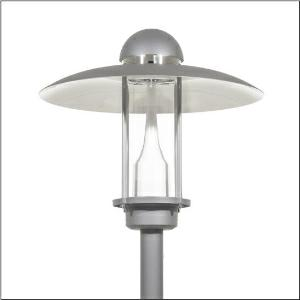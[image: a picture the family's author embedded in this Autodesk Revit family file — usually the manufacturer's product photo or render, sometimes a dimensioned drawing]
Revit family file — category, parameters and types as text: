
# Revit family: city-light_elegance_iq___st1_2a_5xa5265ef14h_e69b
name_source: partatom
category: Lighting Fixtures
units: mm (PartAtom-declared; Revit-internal decimal feet)

## family parameters
Cut with Voids When Loaded = No
Host = Face
Light Source = No
Part Type = Normal
Room Calculation Point = No
Round Connector Dimension = Use Diameter
Shared = No

## types (1)
- --- (1 x LED, 1470 lm, 10.5 W, 3000K)
    Apparent Load = 11 VA
    CIE Flux Codes = 22 62 94 98 100
    Color Rendering = 70
    Color Temperature = 3000K
    Default Elevation = 1800 mm
    Description = City-Light Elegance iQ, mast luminaire, Module 540 iQ-SR, primary light control with 3 zone facetted reflector, of plastic, silver coated, highly specular, structured, primary optical cover: cover, of PMMA, transparent, light distribution: ST1.2a, light emission: direct distribution, primary light characteristic: asymmetric, installation type: post-top, LED, High Power LED, rated luminous flux: 1.470lm, luminous efficacy: 140lm/W, light colour: 730, colour temperature: 3000K, control gear: ECG iQ, control: Auto-Match, Temp-Guard, Lumen-Switch, Night-Set, Smart-Wire, Light-Fading, Desk-Remote (wireless, voltage-free reading and setting of iQ features in the workshop via application-optimized NFC function/RFID function), optimised constant luminous flux control (CLO 2.0), Street-Remote, presetting dimming logarithmic, with terminal, 6-pole, max. 2.5mm², mains connection: 230..240V, AC, 50/60Hz, start of lifetime: 11W, end of service life: 11W, reduction: 5W, luminaire housing, upper part, of aluminium, coated, Siteco® metallic grey (DB 702S), diameter: 750mm, height: 675mm, spigot size: d x l = 76 x 70mm (post-top) | with reducer (optional accessory) 60 x 70mm, post-top mast mounting element, of diecast aluminium, coated, Siteco® metallic grey (DB 702S), Module 540 iQ-SR, traffic white (RAL 9016), equipment: standard, protection rating (complete): IP65, insulation class (complete): insulation class II (safety insulation), certification: CE, ENEC, VDE, packaging unit: 1 piece

Light Distribution: ST1.2a
    Height = 675 mm
    Lamp = 1 x LED
    Lamp Light Flux = 1470 lm
    Lamp Power = 10.5 W
    Lamp count = 1
    Length = 750 mm
    Luminous efficacy = 140 lm/W
    Manufacturer = Siteco
    ModVariant = No
    Model = 5XA5265EF14H
    Number of Poles = 1
    OnlyDefault = Yes
    Power Factor = 1
    Product Name = City-Light Elegance iQ | ST1.2a
    Product group = mast luminaire | pylon top
    ProductGroupID = 6100
    Protection Class = Protection class II
    Protection Degree = IP 65
    RLX_Detail_Level = 1
    RLX_Emergency_Light_Flux = 0 lm
    RLX_Emergency_Type = 0
    RLX_Emergency_Type_DB = No
    RlxData = <blob elided: 99773 chars, md5=989b9606>
    Socket = socket
    Standby Power = 0 W
    System Light Flux = 1470 lm
    System Power = 11 W
    Type Comments = factory setting: luminous flux: 100 % | dim-lin: 254 | 419 mA
    Type Image = l_1006912.jpg
    URL = http://relux.com
    VarID = @adj_092179
    Voltage = 0 V
    Weight = 0.00 kg
    Width = 0 mm  [stored 0 ft]

note: [stored X ft] marks values corroborated as IEEE doubles in the binary element streams (Revit-internal decimal feet)

## geometry (parser evidence)
native form markers: Blend x4, Sweep x9
no freeform markers — native parametric forms only
